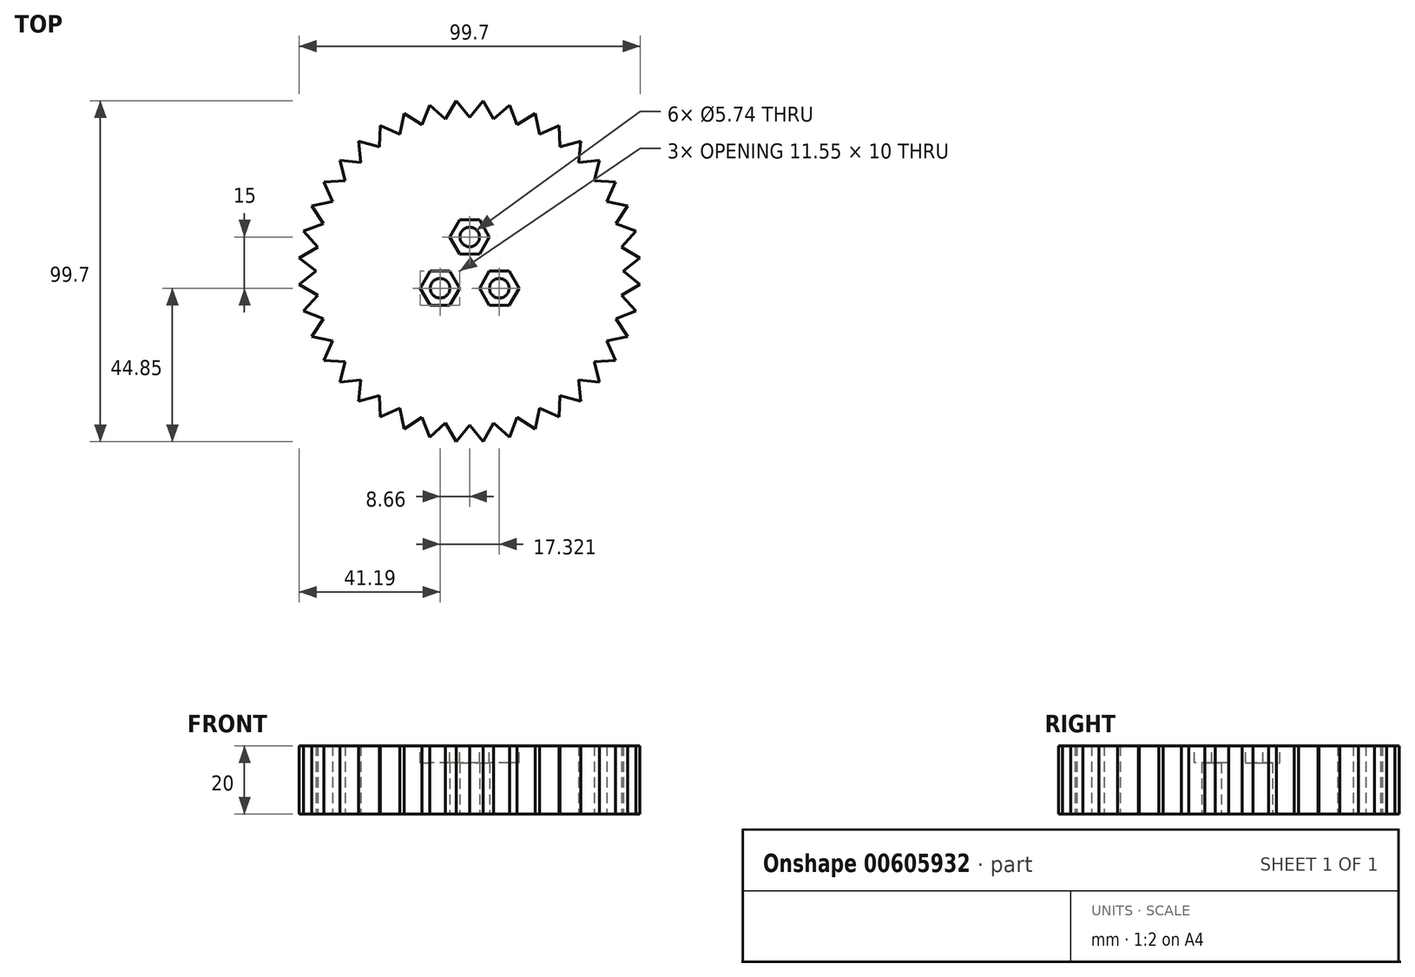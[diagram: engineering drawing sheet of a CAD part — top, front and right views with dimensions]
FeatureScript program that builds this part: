
annotation { "Feature Type Name" : "Feature", "Feature Type Description" : "" }
export const myFeature = defineFeature(function(context is Context, id is Id, definition is map)
    precondition{}
    {
        {
            var Q0;
            Q0=qCreatedBy(makeId("Top.planeOp"),FACE);
            var sketch = newSketch(context, id + "F0", { "sketchPlane" : qUnion([Q0])});
            skCircle(sketch, "E0", {"center": v(0, 0) * mm, "radius": 50 * mm, "construction": true});
            skCircle(sketch, "E1", {"center": v(0, 0) * mm, "radius": 45 * mm, "construction": true});
            skLineSegment(sketch, "E2", {"start": v(0, 0) * mm, "end": v(50, 0) * mm, "construction": true});
            skLineSegment(sketch, "E3", {"start": v(0, 0) * mm, "end": v(49.85, 3.92) * mm, "construction": true});
            skLineSegment(sketch, "E4", {"start": v(0, 0) * mm, "end": v(49.38, 7.82) * mm, "construction": true});
            skLineSegment(sketch, "E5", {"start": v(45, 0) * mm, "end": v(49.85, 3.92) * mm});
            skLineSegment(sketch, "E6", {"start": v(49.85, 3.92) * mm, "end": v(44.45, 7.04) * mm});
            skLineSegment(sketch, "E7.1.0", {"start": v(48.62, 11.67) * mm, "end": v(42.8, 13.9) * mm});
            skLineSegment(sketch, "E7.1.1", {"start": v(44.45, 7.04) * mm, "end": v(48.62, 11.67) * mm});
            skLineSegment(sketch, "E7.2.0", {"start": v(46.2, 19.13) * mm, "end": v(40.1, 20.43) * mm});
            skLineSegment(sketch, "E7.2.1", {"start": v(42.8, 13.9) * mm, "end": v(46.2, 19.13) * mm});
            skLineSegment(sketch, "E7.3.0", {"start": v(42.63, 26.12) * mm, "end": v(36.4, 26.45) * mm});
            skLineSegment(sketch, "E7.3.1", {"start": v(40.1, 20.43) * mm, "end": v(42.63, 26.12) * mm});
            skLineSegment(sketch, "E7.4.0", {"start": v(38.02, 32.47) * mm, "end": v(31.82, 31.82) * mm});
            skLineSegment(sketch, "E7.4.1", {"start": v(36.4, 26.45) * mm, "end": v(38.02, 32.47) * mm});
            skLineSegment(sketch, "E7.5.0", {"start": v(32.47, 38.02) * mm, "end": v(26.45, 36.4) * mm});
            skLineSegment(sketch, "E7.5.1", {"start": v(31.82, 31.82) * mm, "end": v(32.47, 38.02) * mm});
            skLineSegment(sketch, "E7.6.0", {"start": v(26.12, 42.63) * mm, "end": v(20.43, 40.1) * mm});
            skLineSegment(sketch, "E7.6.1", {"start": v(26.45, 36.4) * mm, "end": v(26.12, 42.63) * mm});
            skLineSegment(sketch, "E7.7.0", {"start": v(19.13, 46.2) * mm, "end": v(13.9, 42.8) * mm});
            skLineSegment(sketch, "E7.7.1", {"start": v(20.43, 40.1) * mm, "end": v(19.13, 46.2) * mm});
            skLineSegment(sketch, "E7.8.0", {"start": v(11.67, 48.62) * mm, "end": v(7.04, 44.45) * mm});
            skLineSegment(sketch, "E7.8.1", {"start": v(13.9, 42.8) * mm, "end": v(11.67, 48.62) * mm});
            skLineSegment(sketch, "E7.9.0", {"start": v(3.92, 49.85) * mm, "end": v(0, 45) * mm});
            skLineSegment(sketch, "E7.9.1", {"start": v(7.04, 44.45) * mm, "end": v(3.92, 49.85) * mm});
            skLineSegment(sketch, "E7.10.0", {"start": v(-3.92, 49.85) * mm, "end": v(-7.04, 44.45) * mm});
            skLineSegment(sketch, "E7.10.1", {"start": v(0, 45) * mm, "end": v(-3.92, 49.85) * mm});
            skLineSegment(sketch, "E7.11.0", {"start": v(-11.67, 48.62) * mm, "end": v(-13.9, 42.8) * mm});
            skLineSegment(sketch, "E7.11.1", {"start": v(-7.04, 44.45) * mm, "end": v(-11.67, 48.62) * mm});
            skLineSegment(sketch, "E7.12.0", {"start": v(-19.13, 46.2) * mm, "end": v(-20.43, 40.1) * mm});
            skLineSegment(sketch, "E7.12.1", {"start": v(-13.9, 42.8) * mm, "end": v(-19.13, 46.2) * mm});
            skLineSegment(sketch, "E7.13.0", {"start": v(-26.12, 42.63) * mm, "end": v(-26.45, 36.4) * mm});
            skLineSegment(sketch, "E7.13.1", {"start": v(-20.43, 40.1) * mm, "end": v(-26.12, 42.63) * mm});
            skLineSegment(sketch, "E7.14.0", {"start": v(-32.47, 38.02) * mm, "end": v(-31.82, 31.82) * mm});
            skLineSegment(sketch, "E7.14.1", {"start": v(-26.45, 36.4) * mm, "end": v(-32.47, 38.02) * mm});
            skLineSegment(sketch, "E7.15.0", {"start": v(-38.02, 32.47) * mm, "end": v(-36.4, 26.45) * mm});
            skLineSegment(sketch, "E7.15.1", {"start": v(-31.82, 31.82) * mm, "end": v(-38.02, 32.47) * mm});
            skLineSegment(sketch, "E7.16.0", {"start": v(-42.63, 26.12) * mm, "end": v(-40.1, 20.43) * mm});
            skLineSegment(sketch, "E7.16.1", {"start": v(-36.4, 26.45) * mm, "end": v(-42.63, 26.12) * mm});
            skLineSegment(sketch, "E7.17.0", {"start": v(-46.2, 19.13) * mm, "end": v(-42.8, 13.9) * mm});
            skLineSegment(sketch, "E7.17.1", {"start": v(-40.1, 20.43) * mm, "end": v(-46.2, 19.13) * mm});
            skLineSegment(sketch, "E7.18.0", {"start": v(-48.62, 11.67) * mm, "end": v(-44.45, 7.04) * mm});
            skLineSegment(sketch, "E7.18.1", {"start": v(-42.8, 13.9) * mm, "end": v(-48.62, 11.67) * mm});
            skLineSegment(sketch, "E7.19.0", {"start": v(-49.85, 3.92) * mm, "end": v(-45, 0) * mm});
            skLineSegment(sketch, "E7.19.1", {"start": v(-44.45, 7.04) * mm, "end": v(-49.85, 3.92) * mm});
            skLineSegment(sketch, "E7.20.0", {"start": v(-49.85, -3.92) * mm, "end": v(-44.45, -7.04) * mm});
            skLineSegment(sketch, "E7.20.1", {"start": v(-45, 0) * mm, "end": v(-49.85, -3.92) * mm});
            skLineSegment(sketch, "E7.21.0", {"start": v(-48.62, -11.67) * mm, "end": v(-42.8, -13.9) * mm});
            skLineSegment(sketch, "E7.21.1", {"start": v(-44.45, -7.04) * mm, "end": v(-48.62, -11.67) * mm});
            skLineSegment(sketch, "E7.22.0", {"start": v(-46.2, -19.13) * mm, "end": v(-40.1, -20.43) * mm});
            skLineSegment(sketch, "E7.22.1", {"start": v(-42.8, -13.9) * mm, "end": v(-46.2, -19.13) * mm});
            skLineSegment(sketch, "E7.23.0", {"start": v(-42.63, -26.12) * mm, "end": v(-36.4, -26.45) * mm});
            skLineSegment(sketch, "E7.23.1", {"start": v(-40.1, -20.43) * mm, "end": v(-42.63, -26.12) * mm});
            skLineSegment(sketch, "E7.24.0", {"start": v(-38.02, -32.47) * mm, "end": v(-31.82, -31.82) * mm});
            skLineSegment(sketch, "E7.24.1", {"start": v(-36.4, -26.45) * mm, "end": v(-38.02, -32.47) * mm});
            skLineSegment(sketch, "E7.25.0", {"start": v(-32.47, -38.02) * mm, "end": v(-26.45, -36.4) * mm});
            skLineSegment(sketch, "E7.25.1", {"start": v(-31.82, -31.82) * mm, "end": v(-32.47, -38.02) * mm});
            skLineSegment(sketch, "E7.26.0", {"start": v(-26.12, -42.63) * mm, "end": v(-20.43, -40.1) * mm});
            skLineSegment(sketch, "E7.26.1", {"start": v(-26.45, -36.4) * mm, "end": v(-26.12, -42.63) * mm});
            skLineSegment(sketch, "E7.27.0", {"start": v(-19.13, -46.2) * mm, "end": v(-13.9, -42.8) * mm});
            skLineSegment(sketch, "E7.27.1", {"start": v(-20.43, -40.1) * mm, "end": v(-19.13, -46.2) * mm});
            skLineSegment(sketch, "E7.28.0", {"start": v(-11.67, -48.62) * mm, "end": v(-7.04, -44.45) * mm});
            skLineSegment(sketch, "E7.28.1", {"start": v(-13.9, -42.8) * mm, "end": v(-11.67, -48.62) * mm});
            skLineSegment(sketch, "E7.29.0", {"start": v(-3.92, -49.85) * mm, "end": v(0, -45) * mm});
            skLineSegment(sketch, "E7.29.1", {"start": v(-7.04, -44.45) * mm, "end": v(-3.92, -49.85) * mm});
            skLineSegment(sketch, "E7.30.0", {"start": v(3.92, -49.85) * mm, "end": v(7.04, -44.45) * mm});
            skLineSegment(sketch, "E7.30.1", {"start": v(0, -45) * mm, "end": v(3.92, -49.85) * mm});
            skLineSegment(sketch, "E7.31.0", {"start": v(11.67, -48.62) * mm, "end": v(13.9, -42.8) * mm});
            skLineSegment(sketch, "E7.31.1", {"start": v(7.04, -44.45) * mm, "end": v(11.67, -48.62) * mm});
            skLineSegment(sketch, "E7.32.0", {"start": v(19.13, -46.2) * mm, "end": v(20.43, -40.1) * mm});
            skLineSegment(sketch, "E7.32.1", {"start": v(13.9, -42.8) * mm, "end": v(19.13, -46.2) * mm});
            skLineSegment(sketch, "E7.33.0", {"start": v(26.12, -42.63) * mm, "end": v(26.45, -36.4) * mm});
            skLineSegment(sketch, "E7.33.1", {"start": v(20.43, -40.1) * mm, "end": v(26.12, -42.63) * mm});
            skLineSegment(sketch, "E7.34.0", {"start": v(32.47, -38.02) * mm, "end": v(31.82, -31.82) * mm});
            skLineSegment(sketch, "E7.34.1", {"start": v(26.45, -36.4) * mm, "end": v(32.47, -38.02) * mm});
            skLineSegment(sketch, "E7.35.0", {"start": v(38.02, -32.47) * mm, "end": v(36.4, -26.45) * mm});
            skLineSegment(sketch, "E7.35.1", {"start": v(31.82, -31.82) * mm, "end": v(38.02, -32.47) * mm});
            skLineSegment(sketch, "E7.36.0", {"start": v(42.63, -26.12) * mm, "end": v(40.1, -20.43) * mm});
            skLineSegment(sketch, "E7.36.1", {"start": v(36.4, -26.45) * mm, "end": v(42.63, -26.12) * mm});
            skLineSegment(sketch, "E7.37.0", {"start": v(46.2, -19.13) * mm, "end": v(42.8, -13.9) * mm});
            skLineSegment(sketch, "E7.37.1", {"start": v(40.1, -20.43) * mm, "end": v(46.2, -19.13) * mm});
            skLineSegment(sketch, "E7.38.0", {"start": v(48.62, -11.67) * mm, "end": v(44.45, -7.04) * mm});
            skLineSegment(sketch, "E7.38.1", {"start": v(42.8, -13.9) * mm, "end": v(48.62, -11.67) * mm});
            skLineSegment(sketch, "E7.39.0", {"start": v(49.85, -3.92) * mm, "end": v(45, 0) * mm});
            skLineSegment(sketch, "E7.39.1", {"start": v(44.45, -7.04) * mm, "end": v(49.85, -3.92) * mm});
            skCircle(sketch, "E8", {"center": v(0, 10) * mm, "radius": 2.87 * mm});
            skCircle(sketch, "E9.1.0", {"center": v(-8.66, -5) * mm, "radius": 2.87 * mm});
            skCircle(sketch, "E9.2.0", {"center": v(8.66, -5) * mm, "radius": 2.87 * mm});
            skSolve(sketch);
        }
        {
            var Q0;
            Q0 = qSketchRegion(id + "F0", true);
            extrude(context, id + "F1", {"entities" : qUnion([Q0]), "depth" : 20 * mm, "offsetDistance" : 25 * mm});
        }
        {
            var Q0;
            Q0=makeQuery(id+"F1.opExtrude","CAP_FACE",FACE,{"disambiguationData":[OSD([sQuery(id+"F0.wireOp",EDGE,"E5"),sQuery(id+"F0.wireOp",EDGE,"E6"),sQuery(id+"F0.wireOp",EDGE,"E7.1.0"),sQuery(id+"F0.wireOp",EDGE,"E7.1.1"),sQuery(id+"F0.wireOp",EDGE,"E7.2.0"),sQuery(id+"F0.wireOp",EDGE,"E7.2.1"),sQuery(id+"F0.wireOp",EDGE,"E7.3.0"),sQuery(id+"F0.wireOp",EDGE,"E7.3.1"),sQuery(id+"F0.wireOp",EDGE,"E7.4.0"),sQuery(id+"F0.wireOp",EDGE,"E7.4.1"),sQuery(id+"F0.wireOp",EDGE,"E7.5.0"),sQuery(id+"F0.wireOp",EDGE,"E7.5.1"),sQuery(id+"F0.wireOp",EDGE,"E7.6.0"),sQuery(id+"F0.wireOp",EDGE,"E7.6.1"),sQuery(id+"F0.wireOp",EDGE,"E7.7.0"),sQuery(id+"F0.wireOp",EDGE,"E7.7.1"),sQuery(id+"F0.wireOp",EDGE,"E7.8.0"),sQuery(id+"F0.wireOp",EDGE,"E7.8.1"),sQuery(id+"F0.wireOp",EDGE,"E7.9.0"),sQuery(id+"F0.wireOp",EDGE,"E7.9.1"),sQuery(id+"F0.wireOp",EDGE,"E7.10.0"),sQuery(id+"F0.wireOp",EDGE,"E7.10.1"),sQuery(id+"F0.wireOp",EDGE,"E7.11.0"),sQuery(id+"F0.wireOp",EDGE,"E7.11.1"),sQuery(id+"F0.wireOp",EDGE,"E7.12.0"),sQuery(id+"F0.wireOp",EDGE,"E7.12.1"),sQuery(id+"F0.wireOp",EDGE,"E7.13.0"),sQuery(id+"F0.wireOp",EDGE,"E7.13.1"),sQuery(id+"F0.wireOp",EDGE,"E7.14.0"),sQuery(id+"F0.wireOp",EDGE,"E7.14.1"),sQuery(id+"F0.wireOp",EDGE,"E7.15.0"),sQuery(id+"F0.wireOp",EDGE,"E7.15.1"),sQuery(id+"F0.wireOp",EDGE,"E7.16.0"),sQuery(id+"F0.wireOp",EDGE,"E7.16.1"),sQuery(id+"F0.wireOp",EDGE,"E7.17.0"),sQuery(id+"F0.wireOp",EDGE,"E7.17.1"),sQuery(id+"F0.wireOp",EDGE,"E7.18.0"),sQuery(id+"F0.wireOp",EDGE,"E7.18.1"),sQuery(id+"F0.wireOp",EDGE,"E7.19.0"),sQuery(id+"F0.wireOp",EDGE,"E7.19.1"),sQuery(id+"F0.wireOp",EDGE,"E7.20.0"),sQuery(id+"F0.wireOp",EDGE,"E7.20.1"),sQuery(id+"F0.wireOp",EDGE,"E7.21.0"),sQuery(id+"F0.wireOp",EDGE,"E7.21.1"),sQuery(id+"F0.wireOp",EDGE,"E7.22.0"),sQuery(id+"F0.wireOp",EDGE,"E7.22.1"),sQuery(id+"F0.wireOp",EDGE,"E7.23.0"),sQuery(id+"F0.wireOp",EDGE,"E7.23.1"),sQuery(id+"F0.wireOp",EDGE,"E7.24.0"),sQuery(id+"F0.wireOp",EDGE,"E7.24.1"),sQuery(id+"F0.wireOp",EDGE,"E7.25.0"),sQuery(id+"F0.wireOp",EDGE,"E7.25.1"),sQuery(id+"F0.wireOp",EDGE,"E7.26.0"),sQuery(id+"F0.wireOp",EDGE,"E7.26.1"),sQuery(id+"F0.wireOp",EDGE,"E7.27.0"),sQuery(id+"F0.wireOp",EDGE,"E7.27.1"),sQuery(id+"F0.wireOp",EDGE,"E7.28.0"),sQuery(id+"F0.wireOp",EDGE,"E7.28.1"),sQuery(id+"F0.wireOp",EDGE,"E7.29.0"),sQuery(id+"F0.wireOp",EDGE,"E7.29.1"),sQuery(id+"F0.wireOp",EDGE,"E7.30.0"),sQuery(id+"F0.wireOp",EDGE,"E7.30.1"),sQuery(id+"F0.wireOp",EDGE,"E7.31.0"),sQuery(id+"F0.wireOp",EDGE,"E7.31.1"),sQuery(id+"F0.wireOp",EDGE,"E7.32.0"),sQuery(id+"F0.wireOp",EDGE,"E7.32.1"),sQuery(id+"F0.wireOp",EDGE,"E7.33.0"),sQuery(id+"F0.wireOp",EDGE,"E7.33.1"),sQuery(id+"F0.wireOp",EDGE,"E7.34.0"),sQuery(id+"F0.wireOp",EDGE,"E7.34.1"),sQuery(id+"F0.wireOp",EDGE,"E7.35.0"),sQuery(id+"F0.wireOp",EDGE,"E7.35.1"),sQuery(id+"F0.wireOp",EDGE,"E7.36.0"),sQuery(id+"F0.wireOp",EDGE,"E7.36.1"),sQuery(id+"F0.wireOp",EDGE,"E7.37.0"),sQuery(id+"F0.wireOp",EDGE,"E7.37.1"),sQuery(id+"F0.wireOp",EDGE,"E7.38.0"),sQuery(id+"F0.wireOp",EDGE,"E7.38.1"),sQuery(id+"F0.wireOp",EDGE,"E7.39.0"),sQuery(id+"F0.wireOp",EDGE,"E7.39.1"),sQuery(id+"F0.wireOp",EDGE,"E8"),sQuery(id+"F0.wireOp",EDGE,"E9.1.0"),sQuery(id+"F0.wireOp",EDGE,"E9.2.0")])],"isStart":false});
            var sketch = newSketch(context, id + "F2", { "sketchPlane" : qUnion([Q0])});
            skCircle(sketch, "E10.cCircle", {"center": v(0, 10) * mm, "radius": 5 * mm, "construction": true});
            skLineSegment(sketch, "E10.0", {"start": v(-2.89, 15) * mm, "end": v(2.89, 15) * mm});
            skLineSegment(sketch, "E10.1", {"start": v(2.89, 15) * mm, "end": v(5.77, 10) * mm});
            skLineSegment(sketch, "E10.2", {"start": v(5.77, 10) * mm, "end": v(2.89, 5) * mm});
            skLineSegment(sketch, "E10.3", {"start": v(2.89, 5) * mm, "end": v(-2.89, 5) * mm});
            skLineSegment(sketch, "E10.4", {"start": v(-2.89, 5) * mm, "end": v(-5.77, 10) * mm});
            skLineSegment(sketch, "E10.5", {"start": v(-5.77, 10) * mm, "end": v(-2.89, 15) * mm});
            skPoint(sketch, "E10.0.midPoint", {"position": v(0, 15) * mm});
            skCircle(sketch, "E11.1.0", {"center": v(-8.66, -5) * mm, "radius": 5 * mm, "construction": true});
            skLineSegment(sketch, "E11.1.1", {"start": v(-14.43, -5) * mm, "end": v(-11.55, 0) * mm});
            skLineSegment(sketch, "E11.1.2", {"start": v(-11.55, -10) * mm, "end": v(-14.43, -5) * mm});
            skLineSegment(sketch, "E11.1.3", {"start": v(-5.77, -10) * mm, "end": v(-11.55, -10) * mm});
            skLineSegment(sketch, "E11.1.4", {"start": v(-2.89, -5) * mm, "end": v(-5.77, -10) * mm});
            skLineSegment(sketch, "E11.1.5", {"start": v(-5.77, 0) * mm, "end": v(-2.89, -5) * mm});
            skLineSegment(sketch, "E11.1.6", {"start": v(-11.55, 0) * mm, "end": v(-5.77, 0) * mm});
            skCircle(sketch, "E11.2.0", {"center": v(8.66, -5) * mm, "radius": 5 * mm, "construction": true});
            skLineSegment(sketch, "E11.2.1", {"start": v(11.55, -10) * mm, "end": v(5.77, -10) * mm});
            skLineSegment(sketch, "E11.2.2", {"start": v(14.43, -5) * mm, "end": v(11.55, -10) * mm});
            skLineSegment(sketch, "E11.2.3", {"start": v(11.55, 0) * mm, "end": v(14.43, -5) * mm});
            skLineSegment(sketch, "E11.2.4", {"start": v(5.77, 0) * mm, "end": v(11.55, 0) * mm});
            skLineSegment(sketch, "E11.2.5", {"start": v(2.89, -5) * mm, "end": v(5.77, 0) * mm});
            skLineSegment(sketch, "E11.2.6", {"start": v(5.77, -10) * mm, "end": v(2.89, -5) * mm});
            skPoint(sketch, "E11.center", {"position": v(0, 0) * mm});
            skSolve(sketch);
        }
        {
            var Q0;
            Q0 = qSketchRegion(id + "F2", true);
            extrude(context, id + "F3", {"entities" : qUnion([Q0]), "operationType" : NewBodyOperationType.REMOVE, "oppositeDirection" : true, "depth" : 5 * mm, "offsetDistance" : 25 * mm});
        }
    });
